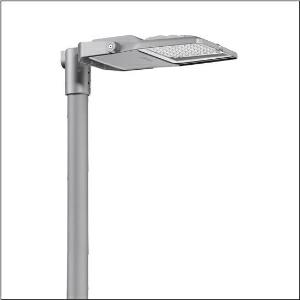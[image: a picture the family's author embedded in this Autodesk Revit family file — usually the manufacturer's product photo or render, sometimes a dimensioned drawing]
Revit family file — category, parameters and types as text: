
# Revit family: floodlight_fl_21_mini___pl61_5xa7776d2c3a_4c8f
name_source: partatom
category: Lighting Fixtures
units: mm (PartAtom-declared; Revit-internal decimal feet)

## family parameters
Cut with Voids When Loaded = No
Host = Face
Light Source = No
Part Type = Normal
Room Calculation Point = No
Round Connector Dimension = Use Diameter
Shared = No

## types (1)
- --- (1 x LED, 17510 lm, 142.9 W, 3000K)
    Apparent Load = 143 VA
    CIE Flux Codes = 33 65 98 100 100
    Color Rendering = 70
    Color Temperature = 3000K
    Default Elevation = 1800 mm
    Description = Floodlight FL 21 mini, floodlight, primary light control with lens, of PMMA, primary optical cover: protective disc, of toughened safety glass, transparent, light distribution: PL61, light emission: direct distribution, installation type: surface-mounted, LED, High Power LED, rated luminous flux: 17.510lm, luminous efficacy: 123lm/W, light colour: 730, colour temperature: 3000K, control gear: Smart Interface (Zhaga), control: flexible luminous flux parameterisation, time-dependent luminous flux control, constant luminous flux control, overheat protection, pre-setting: logarithmic dimming characteristic, with terminal, 6-pole, mains connection: 220..240V, AC, 50/60Hz, start of lifetime: 143W, end of service life: 151W, reduction: 63W, luminaire housing, of diecast aluminium, powder-coated, SITECO metallic grey (DB 702S), corrosivity category C5 mid according to DIN EN ISO 12944, suitable for swimming pools, chlorine-resistant, sealing non-destructively replaceable, please order mast flange separately, mast bracket, of steel, galvanised, powder-coated, SITECO metallic grey (DB 702S), Smart Interface below and above, protection rating (complete): IP66, insulation class (complete): insulation class II (safety insulation), certification: CE, ENEC, VDE, protection symbol: D, impact resistance: IK08, permissible operating ambient temperature: -40..+40°C, permissible operating ambient temperature for outdoor applications: -40..+50°C, standard: DIN EN 12944, LABS conformity tested according to VDMA 24364:2018-05, packaging unit: 1 piece

Light Distribution: PL61
    Height = 70 mm
    Lamp = 1 x LED
    Lamp Light Flux = 17510 lm
    Lamp Power = 142.9 W
    Lamp count = 1
    Length = 485 mm
    Luminous efficacy = 123 lm/W
    Manufacturer = Siteco
    ModVariant = No
    Model = 5XA7776D2C3A
    Mounting Place = Pole
    Mounting Type = Pole annexe
    Number of Poles = 1
    OnlyDefault = Yes
    Power Factor = 1
    Product Name = Floodlight FL 21 mini | PL61
    Product group = floodlight | pylon annexe
    ProductGroupID = 6201
    Protection Class = Protection class II
    Protection Degree = IP 66
    RLX_Detail_Level = 1
    RLX_Emergency_Light_Flux = 0 lm
    RLX_Emergency_Type = 0
    RLX_Emergency_Type_DB = No
    RlxData = <blob elided: 101349 chars, md5=05985bf4>
    Socket = socket
    Standby Power = 0 W
    System Light Flux = 17510 lm
    System Power = 143 W
    Type Comments = factory setting: luminous flux: 100 % | dim-lin: 254 | 730 mA
    Type Image = l_1007125.jpg
    URL = http://relux.com
    VarID = @adj_172887
    Voltage = 0 V
    Weight = 0.00 kg
    Width = 337 mm

## geometry (parser evidence)
native form markers: Blend x4, Sweep x13
no freeform markers — native parametric forms only
